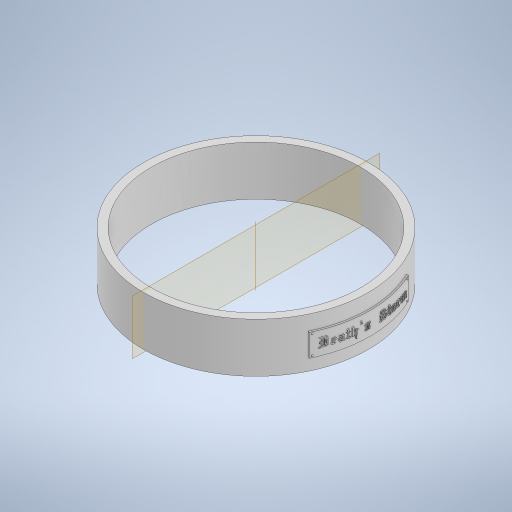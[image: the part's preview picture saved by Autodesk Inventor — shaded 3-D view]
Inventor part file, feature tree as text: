
AUTODESK INVENTOR PART (.ipt)
format: ipt  version: 2023 (Build 270158000, 158)  size: 5,317,120 bytes
history: native  units: in
note: dims shown in document units (in); Inventor stores cm internally (conversion verified against a paired STEP export)
features: emboss x3, pattern_circular x3, other x2, extrude x1, plane x1, fillet x1, sketch x1
ambient origin geometry x8: Origin, YZ Plane, XZ Plane, XY Plane, X Axis, Y Axis, Z Axis, Center Point
bodies: Solid1 (feature_tree)
feature tree (12):
  extrude  "Extrusion1"  Depth=0.3937in
  plane  "Work Plane1"
  other  "Text"
  emboss  "Emboss4"
  emboss  "Emboss5"
  emboss  "Emboss6"
  fillet  "Rivots"  Radius=0.8661in
  pattern_circular  "Circular Pattern1"  Count=6  [1 undecoded]
  pattern_circular  "Circular Pattern2"  [2 undecoded]
  pattern_circular  "Circular Pattern3"  [2 undecoded]
  sketch  "Sketch1"  dims[d0=3.937in d1=3.6614in d2=0.8661in d3=0.0in d4=2.3622in d6=0.4546in d10=0.0in d11=0.3937in d12=1.7717in d19=0.0in d20=0.0in d21=0.0295in d22=0.0in d23=0.0197in d24=0.0in d25=0.0295in d26=0.0295in d27=0.0295in d28=0.0157in d29=0.0in d30=0.0138in d31=0.7874in d32=360.0deg d34=0.7874in d35=360.0deg d37=0.7874in d38=360.0deg d33=0.0in]
  other  "NamePlate"
note: 5 required parameter values undecoded (feature->parameter linkage not recoverable at this tier; creation-order binding heuristic only, values carry confidence <= 0.55)
